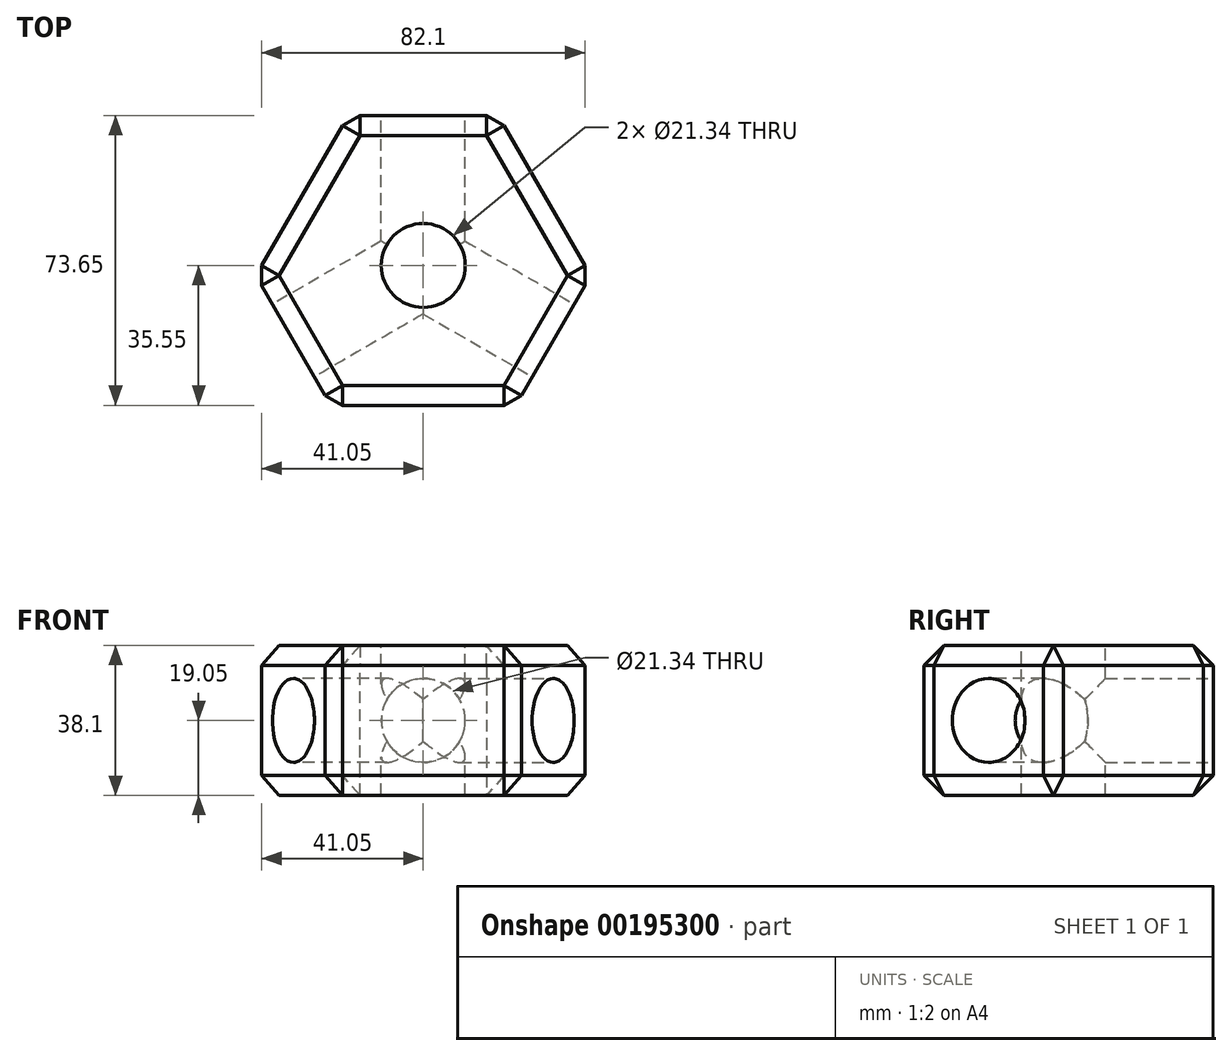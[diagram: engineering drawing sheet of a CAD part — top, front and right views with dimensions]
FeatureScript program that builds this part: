
annotation { "Feature Type Name" : "Feature", "Feature Type Description" : "" }
export const myFeature = defineFeature(function(context is Context, id is Id, definition is map)
    precondition{}
    {
        {
            var Q0;
            Q0=qCreatedBy(makeId("Top.planeOp"),FACE);
            var sketch = newSketch(context, id + "F0", { "sketchPlane" : qUnion([Q0])});
            skLineSegment(sketch, "E0", {"start": v(0, 0) * mm, "end": v(0, 38.1) * mm});
            skLineSegment(sketch, "E1", {"start": v(0, 38.1) * mm, "end": v(19.05, 38.1) * mm});
            skLineSegment(sketch, "E2", {"start": v(19.05, 38.1) * mm, "end": v(0, 0) * mm});
            skLineSegment(sketch, "E3.MirrorCS", {"start": v(-19.05, 38.1) * mm, "end": v(0, 0) * mm});
            skLineSegment(sketch, "E4.MirrorCS", {"start": v(0, 38.1) * mm, "end": v(-19.05, 38.1) * mm});
            skLineSegment(sketch, "E5.1.0", {"start": v(-42.52, -2.55) * mm, "end": v(0, 0) * mm});
            skLineSegment(sketch, "E5.2.0", {"start": v(23.47, -35.55) * mm, "end": v(0, 0) * mm});
            skPoint(sketch, "E5.center", {"position": v(0, 0) * mm});
            skLineSegment(sketch, "E6.1.0", {"start": v(0, 0) * mm, "end": v(-33, -19.05) * mm});
            skLineSegment(sketch, "E6.1.1", {"start": v(-23.47, -35.55) * mm, "end": v(0, 0) * mm});
            skLineSegment(sketch, "E6.1.2", {"start": v(-33, -19.05) * mm, "end": v(-42.52, -2.55) * mm});
            skLineSegment(sketch, "E6.1.3", {"start": v(-33, -19.05) * mm, "end": v(-23.47, -35.55) * mm});
            skLineSegment(sketch, "E6.2.0", {"start": v(0, 0) * mm, "end": v(33, -19.05) * mm});
            skLineSegment(sketch, "E6.2.1", {"start": v(42.52, -2.55) * mm, "end": v(0, 0) * mm});
            skLineSegment(sketch, "E6.2.2", {"start": v(33, -19.05) * mm, "end": v(23.47, -35.55) * mm});
            skLineSegment(sketch, "E6.2.3", {"start": v(33, -19.05) * mm, "end": v(42.52, -2.55) * mm});
            skLineSegment(sketch, "E7", {"start": v(-42.52, -2.55) * mm, "end": v(-19.05, 38.1) * mm});
            skLineSegment(sketch, "E8", {"start": v(19.05, 38.1) * mm, "end": v(42.52, -2.55) * mm});
            skLineSegment(sketch, "E9", {"start": v(-23.47, -35.55) * mm, "end": v(23.47, -35.55) * mm});
            skSolve(sketch);
        }
        {
            var Q0;
            Q0=makeQuery(id+"F0.imprint","IMPRINT",FACE,{"disambiguationData":[TD([[makeQuery(id+"F0.imprint","IMPRINT",EDGE,{"derivedFrom":sQuery(id+"F0.wireOp",EDGE,"E0")}),1.0]])]});
            var Q1;
            Q1=makeQuery(id+"F0.imprint","IMPRINT",FACE,{"disambiguationData":[TD([[makeQuery(id+"F0.imprint","IMPRINT",EDGE,{"derivedFrom":sQuery(id+"F0.wireOp",EDGE,"E0")}),-1.0]])]});
            var Q2;
            Q2=makeQuery(id+"F0.imprint","IMPRINT",FACE,{"disambiguationData":[TD([[makeQuery(id+"F0.imprint","IMPRINT",EDGE,{"derivedFrom":sQuery(id+"F0.wireOp",EDGE,"E3.MirrorCS")}),-1.0]])]});
            var Q3;
            Q3=makeQuery(id+"F0.imprint","IMPRINT",FACE,{"disambiguationData":[TD([[makeQuery(id+"F0.imprint","IMPRINT",EDGE,{"derivedFrom":sQuery(id+"F0.wireOp",EDGE,"E2")}),1.0]])]});
            var Q4;
            Q4=makeQuery(id+"F0.imprint","IMPRINT",FACE,{"disambiguationData":[TD([[makeQuery(id+"F0.imprint","IMPRINT",EDGE,{"derivedFrom":sQuery(id+"F0.wireOp",EDGE,"E5.1.0")}),-1.0]])]});
            var Q5;
            Q5=makeQuery(id+"F0.imprint","IMPRINT",FACE,{"disambiguationData":[TD([[makeQuery(id+"F0.imprint","IMPRINT",EDGE,{"derivedFrom":sQuery(id+"F0.wireOp",EDGE,"E6.1.0")}),1.0]])]});
            var Q6;
            Q6=makeQuery(id+"F0.imprint","IMPRINT",FACE,{"disambiguationData":[TD([[makeQuery(id+"F0.imprint","IMPRINT",EDGE,{"derivedFrom":sQuery(id+"F0.wireOp",EDGE,"E5.2.0")}),1.0]])]});
            var Q7;
            Q7=makeQuery(id+"F0.imprint","IMPRINT",FACE,{"disambiguationData":[TD([[makeQuery(id+"F0.imprint","IMPRINT",EDGE,{"derivedFrom":sQuery(id+"F0.wireOp",EDGE,"E5.2.0")}),-1.0]])]});
            var Q8;
            Q8=makeQuery(id+"F0.imprint","IMPRINT",FACE,{"disambiguationData":[TD([[makeQuery(id+"F0.imprint","IMPRINT",EDGE,{"derivedFrom":sQuery(id+"F0.wireOp",EDGE,"E6.2.0")}),1.0]])]});
            extrude(context, id + "F1", {"entities" : qUnion([Q0, Q1, Q2, Q3, Q4, Q5, Q6, Q7, Q8]), "depth" : 38.1 * mm});
        }
        {
            var Q0;
            Q0=makeQuery(id+"F1.opExtrude","SWEPT_FACE",FACE,{"disambiguationData":[OSD([sQuery(id+"F0.wireOp",EDGE,"E6.1.2"),sQuery(id+"F0.wireOp",EDGE,"E6.1.3")])]});
            var sketch = newSketch(context, id + "F2", { "sketchPlane" : qUnion([Q0])});
            skLineSegment(sketch, "E10", {"start": v(-19.05, 38.1) * mm, "end": v(0, 38.1) * mm});
            skLineSegment(sketch, "E11", {"start": v(0, 38.1) * mm, "end": v(0, 19.05) * mm});
            skCircle(sketch, "E12", {"center": v(0, 19.05) * mm, "radius": 10.67 * mm});
            skSolve(sketch);
        }
        {
            var Q0;
            Q0=makeQuery(id+"F2.imprint","IMPRINT",FACE,{"disambiguationData":[TD([[makeQuery(id+"F2.imprint","IMPRINT",EDGE,{"derivedFrom":sQuery(id+"F2.wireOp",EDGE,"E12")}),1.0]])]});
            extrude(context, id + "F3", {"entities" : qUnion([Q0]), "operationType" : NewBodyOperationType.REMOVE, "oppositeDirection" : true, "depth" : 44.45 * mm});
        }
        {
            var Q0;
            Q0=makeQuery(id+"F1.opExtrude","SWEPT_FACE",FACE,{"disambiguationData":[OSD([sQuery(id+"F0.wireOp",EDGE,"E6.2.2"),sQuery(id+"F0.wireOp",EDGE,"E6.2.3")])]});
            var sketch = newSketch(context, id + "F4", { "sketchPlane" : qUnion([Q0])});
            skLineSegment(sketch, "E13", {"start": v(-19.05, 38.1) * mm, "end": v(0, 38.1) * mm});
            skLineSegment(sketch, "E14", {"start": v(0, 38.1) * mm, "end": v(0, 19.05) * mm});
            skCircle(sketch, "E15", {"center": v(0, 19.05) * mm, "radius": 10.67 * mm});
            skSolve(sketch);
        }
        {
            var Q0;
            Q0=makeQuery(id+"F4.imprint","IMPRINT",FACE,{"disambiguationData":[TD([[makeQuery(id+"F4.imprint","IMPRINT",EDGE,{"derivedFrom":sQuery(id+"F4.wireOp",EDGE,"E15")}),1.0]])]});
            extrude(context, id + "F5", {"entities" : qUnion([Q0]), "operationType" : NewBodyOperationType.REMOVE, "oppositeDirection" : true, "depth" : 44.45 * mm});
        }
        {
            var Q0;
            Q0=makeQuery(id+"F1.opExtrude","SWEPT_FACE",FACE,{"disambiguationData":[OSD([sQuery(id+"F0.wireOp",EDGE,"E1"),sQuery(id+"F0.wireOp",EDGE,"E4.MirrorCS")])]});
            var sketch = newSketch(context, id + "F6", { "sketchPlane" : qUnion([Q0])});
            skLineSegment(sketch, "E16", {"start": v(0, 38.1) * mm, "end": v(0, 19.05) * mm});
            skPoint(sketch, "E16.endSnap0", {"position": v(0, 38.1) * mm});
            skCircle(sketch, "E17", {"center": v(0, 19.05) * mm, "radius": 10.67 * mm});
            skSolve(sketch);
        }
        {
            var Q0;
            Q0=makeQuery(id+"F6.imprint","IMPRINT",FACE,{"disambiguationData":[TD([[makeQuery(id+"F6.imprint","IMPRINT",EDGE,{"derivedFrom":sQuery(id+"F6.wireOp",EDGE,"E17")}),1.0]])]});
            extrude(context, id + "F7", {"entities" : qUnion([Q0]), "operationType" : NewBodyOperationType.REMOVE, "oppositeDirection" : true, "depth" : 44.45 * mm});
        }
        {
            var Q0;
            Q0=makeQuery(id+"F1.opExtrude","CAP_FACE",FACE,{"disambiguationData":[OSD([sQuery(id+"F0.wireOp",EDGE,"E1"),sQuery(id+"F0.wireOp",EDGE,"E4.MirrorCS"),sQuery(id+"F0.wireOp",EDGE,"E6.1.2"),sQuery(id+"F0.wireOp",EDGE,"E6.1.3"),sQuery(id+"F0.wireOp",EDGE,"E6.2.2"),sQuery(id+"F0.wireOp",EDGE,"E6.2.3"),sQuery(id+"F0.wireOp",EDGE,"E7"),sQuery(id+"F0.wireOp",EDGE,"E8"),sQuery(id+"F0.wireOp",EDGE,"E9")])],"isStart":false});
            var sketch = newSketch(context, id + "F8", { "sketchPlane" : qUnion([Q0])});
            skCircle(sketch, "E18", {"center": v(0, 0) * mm, "radius": 10.67 * mm});
            skSolve(sketch);
        }
        {
            var Q0;
            Q0=makeQuery(id+"F8.imprint","IMPRINT",FACE,{"disambiguationData":[TD([[makeQuery(id+"F8.imprint","IMPRINT",EDGE,{"derivedFrom":sQuery(id+"F8.wireOp",EDGE,"E18")}),1.0]])]});
            extrude(context, id + "F9", {"entities" : qUnion([Q0]), "operationType" : NewBodyOperationType.REMOVE, "oppositeDirection" : true, "depth" : 50.8 * mm});
        }
        {
            var Q0;
            Q0=makeQuery(id+"F1.opExtrude","CAP_EDGE",EDGE,{"disambiguationData":[OSD([sQuery(id+"F0.wireOp",EDGE,"E9")])],"isStart":false});
            var Q1;
            Q1=makeQuery(id+"F1.opExtrude","SWEPT_EDGE",EDGE,{"disambiguationData":[OSD([sQuery(id+"F0.wireOp",EDGE,"E6.1.1"),sQuery(id+"F0.wireOp",EDGE,"E6.1.3"),sQuery(id+"F0.wireOp",EDGE,"E9")])]});
            var Q2;
            Q2=makeQuery(id+"F1.opExtrude","CAP_EDGE",EDGE,{"disambiguationData":[OSD([sQuery(id+"F0.wireOp",EDGE,"E6.1.2"),sQuery(id+"F0.wireOp",EDGE,"E6.1.3")])],"isStart":false});
            var Q3;
            Q3=makeQuery(id+"F1.opExtrude","SWEPT_EDGE",EDGE,{"disambiguationData":[OSD([sQuery(id+"F0.wireOp",EDGE,"E5.1.0"),sQuery(id+"F0.wireOp",EDGE,"E6.1.2"),sQuery(id+"F0.wireOp",EDGE,"E7")])]});
            var Q4;
            Q4=makeQuery(id+"F1.opExtrude","CAP_EDGE",EDGE,{"disambiguationData":[OSD([sQuery(id+"F0.wireOp",EDGE,"E6.1.2"),sQuery(id+"F0.wireOp",EDGE,"E6.1.3")])],"isStart":true});
            var Q5;
            Q5=makeQuery(id+"F1.opExtrude","SWEPT_FACE",FACE,{"disambiguationData":[OSD([sQuery(id+"F0.wireOp",EDGE,"E9")])]});
            var Q6;
            Q6=makeQuery(id+"F1.opExtrude","SWEPT_FACE",FACE,{"disambiguationData":[OSD([sQuery(id+"F0.wireOp",EDGE,"E8")])]});
            var Q7;
            Q7=makeQuery(id+"F1.opExtrude","SWEPT_FACE",FACE,{"disambiguationData":[OSD([sQuery(id+"F0.wireOp",EDGE,"E7")])]});
            var Q8;
            Q8=makeQuery(id+"F1.opExtrude","CAP_EDGE",EDGE,{"disambiguationData":[OSD([sQuery(id+"F0.wireOp",EDGE,"E1"),sQuery(id+"F0.wireOp",EDGE,"E4.MirrorCS")])],"isStart":false});
            var Q9;
            Q9=makeQuery(id+"F1.opExtrude","CAP_EDGE",EDGE,{"disambiguationData":[OSD([sQuery(id+"F0.wireOp",EDGE,"E1"),sQuery(id+"F0.wireOp",EDGE,"E4.MirrorCS")])],"isStart":true});
            var Q10;
            Q10=makeQuery(id+"F1.opExtrude","CAP_EDGE",EDGE,{"disambiguationData":[OSD([sQuery(id+"F0.wireOp",EDGE,"E6.2.2"),sQuery(id+"F0.wireOp",EDGE,"E6.2.3")])],"isStart":false});
            var Q11;
            Q11=makeQuery(id+"F1.opExtrude","CAP_EDGE",EDGE,{"disambiguationData":[OSD([sQuery(id+"F0.wireOp",EDGE,"E6.2.2"),sQuery(id+"F0.wireOp",EDGE,"E6.2.3")])],"isStart":true});
            chamfer(context, id + "F10", {"entities" : qUnion([Q0, Q1, Q2, Q3, Q4, Q5, Q6, Q7, Q8, Q9, Q10, Q11]), "width" : 5.08 * mm, "tangentPropagation" : true});
        }
    });
